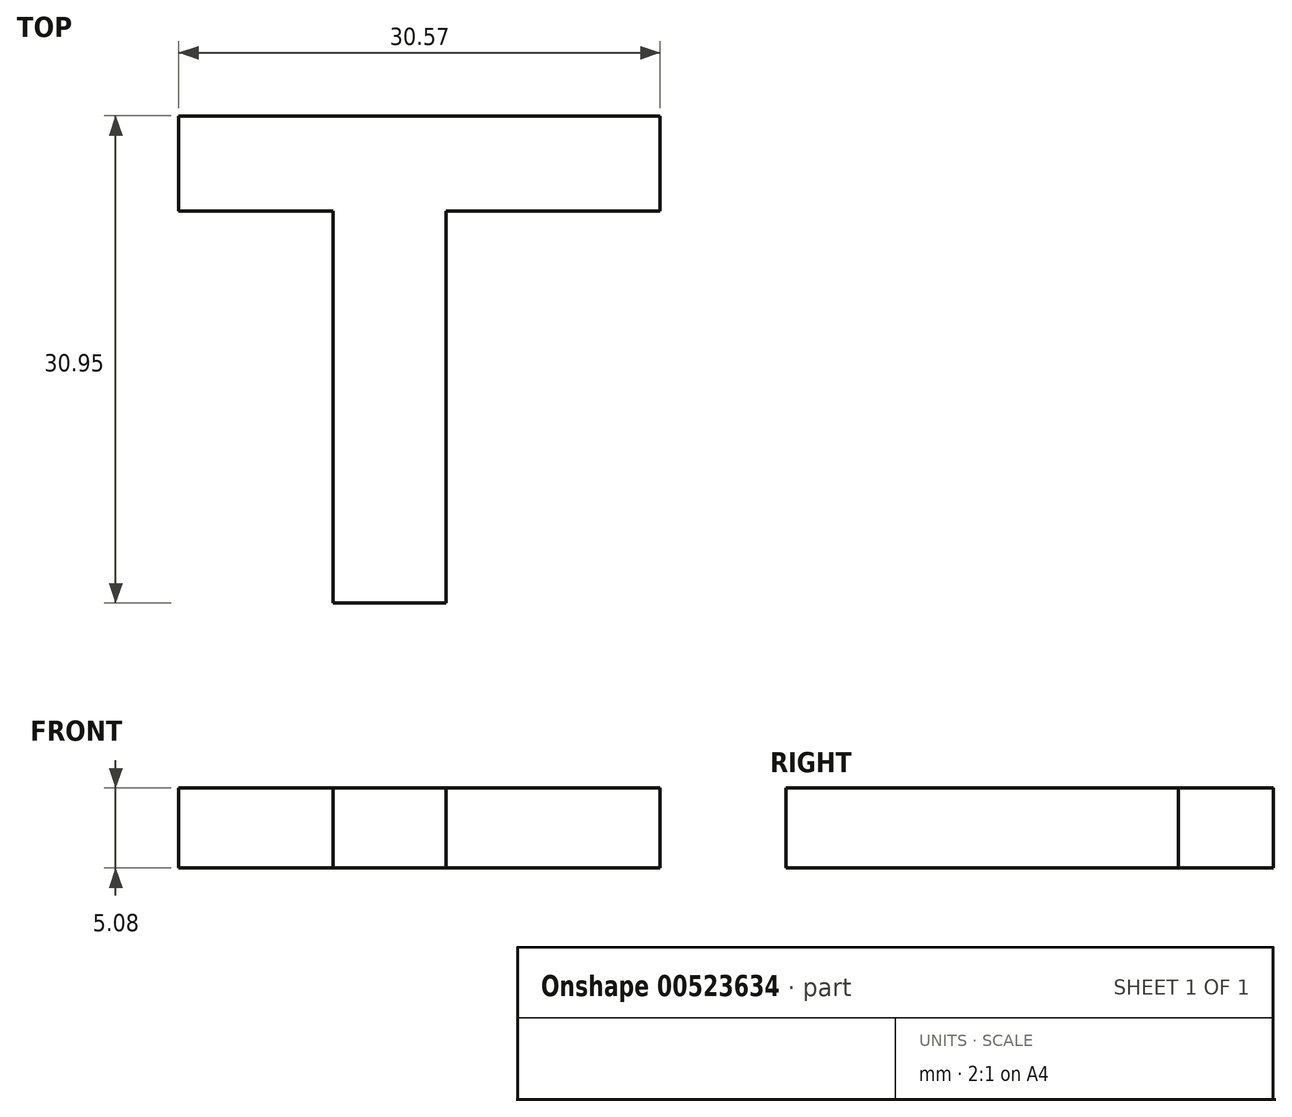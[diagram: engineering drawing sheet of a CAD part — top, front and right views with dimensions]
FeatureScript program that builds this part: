
annotation { "Feature Type Name" : "Feature", "Feature Type Description" : "" }
export const myFeature = defineFeature(function(context is Context, id is Id, definition is map)
    precondition{}
    {
        {
            var Q0;
            Q0=qCreatedBy(makeId("Top.planeOp"),FACE);
            var sketch = newSketch(context, id + "F0", { "sketchPlane" : qUnion([Q0])});
            skLineSegment(sketch, "E0", {"start": v(-45.85, 39.63) * mm, "end": v(-15.28, 39.63) * mm});
            skLineSegment(sketch, "E1", {"start": v(-15.28, 39.63) * mm, "end": v(-15.28, 33.59) * mm});
            skLineSegment(sketch, "E2", {"start": v(-15.28, 33.59) * mm, "end": v(-45.85, 33.59) * mm});
            skLineSegment(sketch, "E3", {"start": v(-45.85, 33.59) * mm, "end": v(-45.85, 39.63) * mm});
            skLineSegment(sketch, "E4", {"start": v(-36.04, 33.59) * mm, "end": v(-36.04, 8.68) * mm});
            skLineSegment(sketch, "E5", {"start": v(-36.04, 8.68) * mm, "end": v(-28.87, 8.68) * mm});
            skLineSegment(sketch, "E6", {"start": v(-28.87, 8.68) * mm, "end": v(-28.87, 33.59) * mm});
            skSolve(sketch);
        }
        {
            var Q0;
            {var subQ0=sQuery(id+"F0.wireOp",EDGE,"E4");Q0=makeQuery(id+"F0.imprint","IMPRINT",FACE,{"disambiguationData":[TD([[makeQuery(id+"F0.imprint","IMPRINT",EDGE,{"derivedFrom":subQ0}),1.0]])]});}
            var Q1;
            Q1=makeQuery(id+"F0.imprint","IMPRINT",FACE,{"disambiguationData":[TD([[makeQuery(id+"F0.imprint","IMPRINT",EDGE,{"derivedFrom":sQuery(id+"F0.wireOp",EDGE,"E0")}),-1.0]])]});
            extrude(context, id + "F1", {"entities" : qUnion([Q0, Q1]), "depth" : 5.08 * mm, "offsetDistance" : 25.4 * mm});
        }
        {
            var Q0;
            Q0=qCreatedBy(makeId("Top.planeOp"),FACE);
            var sketch = newSketch(context, id + "F2", { "sketchPlane" : qUnion([Q0])});
            skCircle(sketch, "E7", {"center": v(5.85, 21.13) * mm, "radius": 13.98 * mm});
            skCircle(sketch, "E8", {"center": v(5.85, 21.13) * mm, "radius": 17.88 * mm});
            skSolve(sketch);
        }
        {
            var Q0;
            Q0=sQuery(id+"F2.wireOp",EDGE,"E8");
            var Q1;
            Q1=sQuery(id+"F2.wireOp",EDGE,"E7");
            extrude(context, id + "F3", {"bodyType" : ToolBodyType.SURFACE, "surfaceEntities" : qUnion([Q0, Q1]), "depth" : 7.62 * mm, "offsetDistance" : 25.4 * mm});
        }
    });
